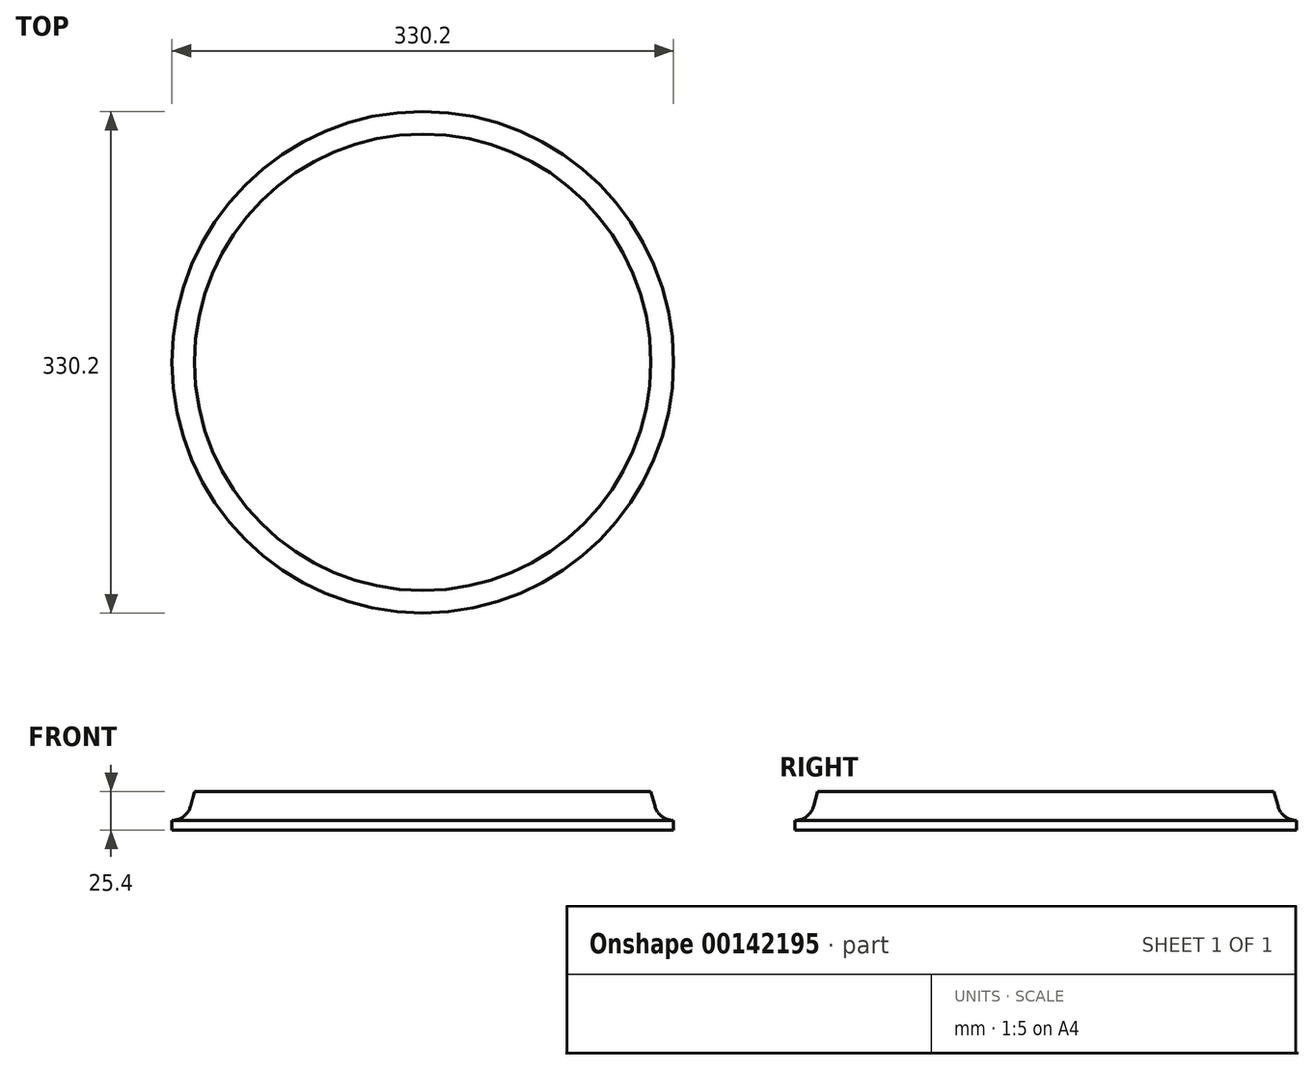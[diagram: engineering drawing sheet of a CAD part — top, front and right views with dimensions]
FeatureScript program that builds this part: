
annotation { "Feature Type Name" : "Feature", "Feature Type Description" : "" }
export const myFeature = defineFeature(function(context is Context, id is Id, definition is map)
    precondition{}
    {
        {
            var Q0;
            Q0=qCreatedBy(makeId("Front.planeOp"),FACE);
            var sketch = newSketch(context, id + "F0", { "sketchPlane" : qUnion([Q0])});
            skLineSegment(sketch, "E0", {"start": v(0, 0) * mm, "end": v(0, 124.84) * mm, "construction": true});
            skLineSegment(sketch, "E1.bottom", {"start": v(0, 0) * mm, "end": v(165.1, 0) * mm});
            skLineSegment(sketch, "E1.top", {"start": v(0, 25.4) * mm, "end": v(150.25, 25.4) * mm});
            skLineSegment(sketch, "E1.left", {"start": v(0, 0) * mm, "end": v(0, 25.4) * mm});
            skLineSegment(sketch, "E1.right", {"start": v(165.1, 0) * mm, "end": v(165.1, 6.35) * mm});
            skLineSegment(sketch, "E2", {"start": v(150.25, 25.4) * mm, "end": v(152.83, 15.76) * mm});
            skArc(sketch, "E3", {"start": v(152.83, 15.76) * mm, "mid": v(157.37, 8.97) * mm, "end": v(165.1, 6.35) * mm});
            skSolve(sketch);
        }
        {
            var Q0;
            Q0 = qSketchRegion(id + "F0", true);
            var Q1;
            Q1=sQuery(id+"F0.wireOp",EDGE,"E0");
            revolve(context, id + "F1", {"entities" : qUnion([Q0]), "axis" : qUnion([Q1]), "revolveType" : RevolveType.FULL});
        }
    });
